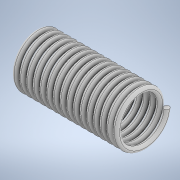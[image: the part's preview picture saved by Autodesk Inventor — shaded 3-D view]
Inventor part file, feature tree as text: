
AUTODESK INVENTOR PART (.ipt)
format: ipt  version: 2021 (Build 250183000, 183)  size: 1,754,624 bytes
history: native  units: in
note: dims shown in document units (in); Inventor stores cm internally (conversion verified against a paired STEP export)
features: helix x1, sketch x1
ambient origin geometry x8: Origin, YZ Plane, XZ Plane, XY Plane, X Axis, Y Axis, Z Axis, Center Point
bodies: Solid1 (feature_tree)
feature tree (2):
  helix  "Coil1"  [1 undecoded]
  sketch  "Sketch1"  dims[d1=0.1378in d2=4.7976in d3=0.6378in d4=6.2992in d5=0.0in d6=90.0deg d7=90.0deg d8=0.0in d9=0.0in]
note: 1 required parameter value undecoded (feature->parameter linkage not recoverable at this tier; creation-order binding heuristic only, values carry confidence <= 0.55)
